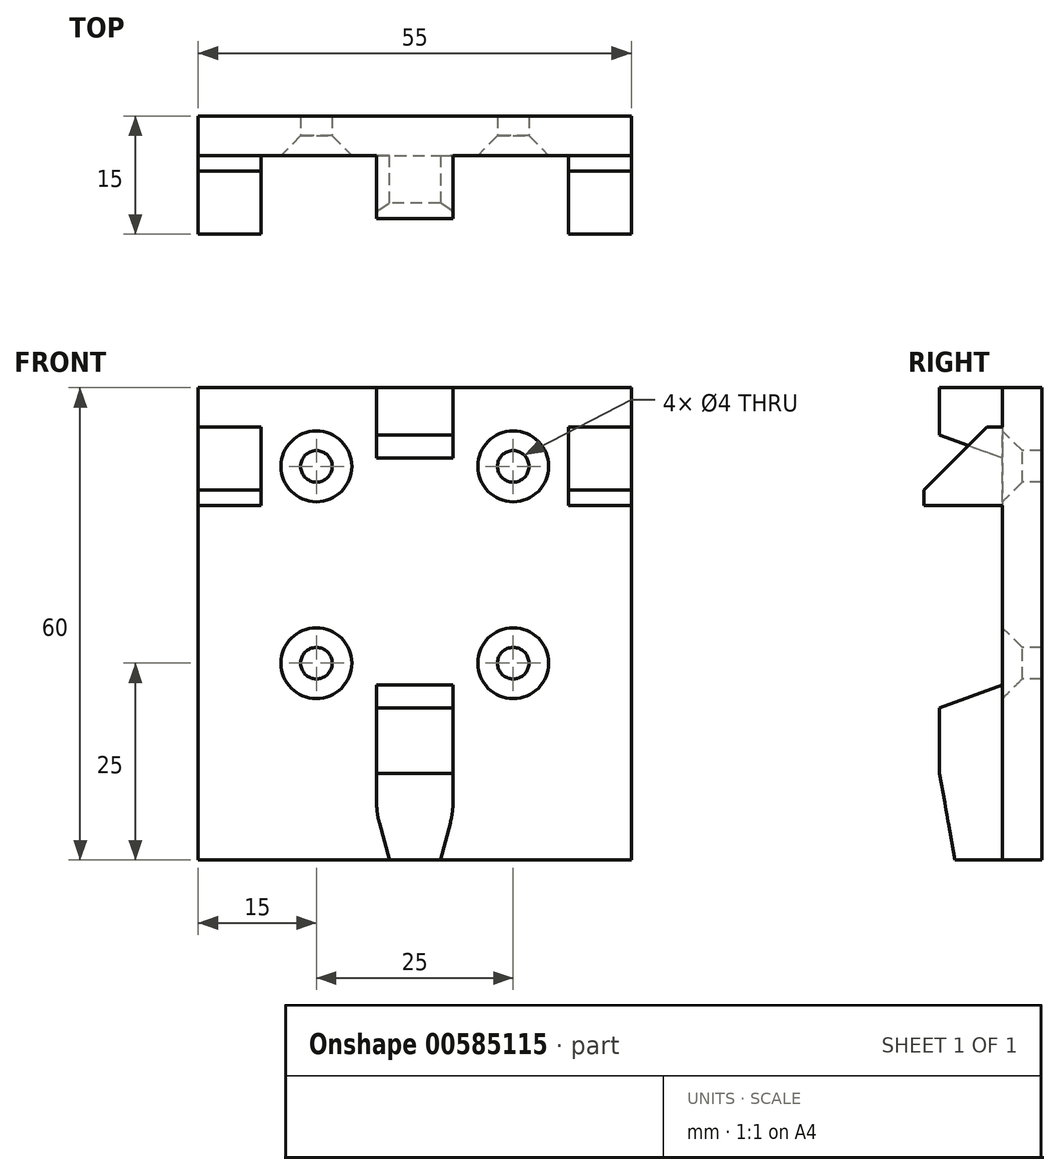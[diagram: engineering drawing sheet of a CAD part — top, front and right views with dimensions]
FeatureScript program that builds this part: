
annotation { "Feature Type Name" : "Feature", "Feature Type Description" : "" }
export const myFeature = defineFeature(function(context is Context, id is Id, definition is map)
    precondition{}
    {
        {
            var Q0;
            Q0=qCreatedBy(makeId("Top.planeOp"),FACE);
            var sketch = newSketch(context, id + "F0", { "sketchPlane" : qUnion([Q0])});
            skLineSegment(sketch, "E0", {"start": v(27.5, 0) * mm, "end": v(27.5, 5) * mm});
            skLineSegment(sketch, "E1", {"start": v(27.5, 5) * mm, "end": v(-27.5, 5) * mm});
            skLineSegment(sketch, "E2", {"start": v(-27.5, 5) * mm, "end": v(-27.5, 0) * mm});
            skLineSegment(sketch, "E3", {"start": v(-4.85, -8) * mm, "end": v(4.85, -8) * mm});
            skPoint(sketch, "E4", {"position": v(0, 0) * mm});
            skLineSegment(sketch, "E5", {"start": v(-4.85, -8) * mm, "end": v(-4.85, 0) * mm});
            skLineSegment(sketch, "E6", {"start": v(-4.85, 0) * mm, "end": v(-27.5, 0) * mm});
            skLineSegment(sketch, "E7", {"start": v(4.85, -8) * mm, "end": v(4.85, 0) * mm});
            skLineSegment(sketch, "E8", {"start": v(4.85, 0) * mm, "end": v(27.5, 0) * mm});
            skLineSegment(sketch, "E9", {"start": v(0, -8) * mm, "end": v(0, 0) * mm, "construction": true});
            skSolve(sketch);
        }
        {
            var Q0;
            Q0=qSketchRegion(id+"F0",true);
            extrude(context, id + "F1", {"entities" : qUnion([Q0]), "depth" : 60 * mm, "offsetDistance" : 25 * mm});
        }
        {
            var Q0;
            Q0=makeQuery(id+"F1.opExtrude","SWEPT_FACE",FACE,{"disambiguationData":[OSD([sQuery(id+"F0.wireOp",EDGE,"E6")])]});
            var sketch = newSketch(context, id + "F2", { "sketchPlane" : qUnion([Q0])});
            skPoint(sketch, "E10", {"position": v(-12.5, 50) * mm});
            skPoint(sketch, "E11", {"position": v(-12.5, 25) * mm});
            skLineSegment(sketch, "E12.bottom", {"start": v(-12.5, 50) * mm, "end": v(12.5, 50) * mm});
            skLineSegment(sketch, "E12.top", {"start": v(-12.5, 25) * mm, "end": v(12.5, 25) * mm});
            skLineSegment(sketch, "E12.left", {"start": v(-12.5, 50) * mm, "end": v(-12.5, 25) * mm});
            skLineSegment(sketch, "E12.right", {"start": v(12.5, 50) * mm, "end": v(12.5, 25) * mm});
            skLineSegment(sketch, "E13", {"start": v(0, 0) * mm, "end": v(0, 25) * mm});
            skPoint(sketch, "E14", {"position": v(0, 25) * mm});
            skPoint(sketch, "E15", {"position": v(12.5, 50) * mm});
            skPoint(sketch, "E16", {"position": v(12.5, 25) * mm});
            skSolve(sketch);
        }
        {
            var Q0;
            Q0=sQuery(id+"F2.wireOp",VERTEX,"E10");
            var Q1;
            Q1=sQuery(id+"F2.wireOp",VERTEX,"E11");
            var Q2;
            Q2=sQuery(id+"F2.wireOp",VERTEX,"E15");
            var Q3;
            Q3=sQuery(id+"F2.wireOp",VERTEX,"E16");
            var Q4;
            Q4=makeQuery(id+"F1.opExtrude","SWEPT_BODY",BODY,{"disambiguationData":[OSD([sQuery(id+"F0.wireOp",EDGE,"E0"),sQuery(id+"F0.wireOp",EDGE,"E1"),sQuery(id+"F0.wireOp",EDGE,"E2"),sQuery(id+"F0.wireOp",EDGE,"E3"),sQuery(id+"F0.wireOp",EDGE,"E5"),sQuery(id+"F0.wireOp",EDGE,"E6"),sQuery(id+"F0.wireOp",EDGE,"E7"),sQuery(id+"F0.wireOp",EDGE,"E8")])]});
            hole(context, id + "F3", {"style" : HoleStyle.C_SINK, "endStyle" : HoleEndStyle.THROUGH, "holeDiameter" : 4 * mm, "cSinkDiameter" : 9 * mm, "cSinkAngle" : 90 * degree, "majorDiameter" : 5 * mm, "isTappedThrough" : true, "tappedDepth" : 12 * mm, "tapClearance" : 3, "locations" : qUnion([Q0, Q1, Q2, Q3]), "scope" : qUnion([Q4])});
        }
        {
            var Q0;
            Q0=makeQuery(id+"F1.opExtrude","CAP_EDGE",EDGE,{"disambiguationData":[OSD([sQuery(id+"F0.wireOp",EDGE,"nqP1lGa1-t7VV-MA4u-jtXe-7mKQE282fZzU")])],"isStart":false});
            var Q1;
            Q1=makeQuery(id+"F1.opExtrude","CAP_EDGE",EDGE,{"disambiguationData":[OSD([sQuery(id+"F0.wireOp",EDGE,"LDgyhp3F-4NZv-x4su-AgHX-1yxxAMKI0rfL")])],"isStart":false});
            var Q2;
            Q2=makeQuery(id+"F1.opExtrude","CAP_EDGE",EDGE,{"disambiguationData":[OSD([sQuery(id+"F0.wireOp",EDGE,"E7")])],"isStart":true});
            var Q3;
            Q3=makeQuery(id+"F1.opExtrude","CAP_EDGE",EDGE,{"disambiguationData":[OSD([sQuery(id+"F0.wireOp",EDGE,"E5")])],"isStart":true});
            chamfer(context, id + "F4", {"entities" : qUnion([Q0, Q1, Q2, Q3]), "chamferType" : ChamferType.OFFSET_ANGLE, "width" : 6 * mm, "oppositeDirection" : false, "angle" : 15 * degree, "tangentPropagation" : true});
        }
        {
            var Q0;
            Q0=makeQuery(id+"F1.opExtrude","SWEPT_FACE",FACE,{"disambiguationData":[OSD([sQuery(id+"F0.wireOp",EDGE,"E6")])]});
            var sketch = newSketch(context, id + "F5", { "sketchPlane" : qUnion([Q0])});
            skLineSegment(sketch, "E17.bottom", {"start": v(-27.5, 55) * mm, "end": v(-19.5, 55) * mm});
            skLineSegment(sketch, "E17.top", {"start": v(-27.5, 45) * mm, "end": v(-19.5, 45) * mm});
            skLineSegment(sketch, "E17.left", {"start": v(-27.5, 55) * mm, "end": v(-27.5, 45) * mm});
            skLineSegment(sketch, "E17.right", {"start": v(-19.5, 55) * mm, "end": v(-19.5, 45) * mm});
            skLineSegment(sketch, "E18.bottom", {"start": v(27.5, 55) * mm, "end": v(19.5, 55) * mm});
            skLineSegment(sketch, "E18.top", {"start": v(27.5, 45) * mm, "end": v(19.5, 45) * mm});
            skLineSegment(sketch, "E18.left", {"start": v(27.5, 55) * mm, "end": v(27.5, 45) * mm});
            skLineSegment(sketch, "E18.right", {"start": v(19.5, 55) * mm, "end": v(19.5, 45) * mm});
            skLineSegment(sketch, "E19", {"start": v(-27.5, 30) * mm, "end": v(-7.31, 30) * mm, "construction": true});
            skSolve(sketch);
        }
        {
            var Q0;
            {var subQ0=sQuery(id+"F0.wireOp",EDGE,"E5");Q0=makeQuery(id+"F4.opChamfer","BLEND_EDGE",EDGE,{"blendedFrom":[makeQuery(id+"F1.opExtrude","CAP_EDGE",EDGE,{"disambiguationData":[OSD([subQ0])],"isStart":true}),makeQuery(id+"F1.opExtrude","SWEPT_FACE",FACE,{"disambiguationData":[OSD([subQ0])]})],"blendedInto":[makeQuery(id+"F1.opExtrude","SWEPT_FACE",FACE,{"disambiguationData":[OSD([subQ0])]})]});}
            var Q1;
            {var subQ0=sQuery(id+"F0.wireOp",EDGE,"E7");Q1=makeQuery(id+"F4.opChamfer","BLEND_EDGE",EDGE,{"blendedFrom":[makeQuery(id+"F1.opExtrude","CAP_EDGE",EDGE,{"disambiguationData":[OSD([subQ0])],"isStart":true}),makeQuery(id+"F1.opExtrude","SWEPT_FACE",FACE,{"disambiguationData":[OSD([subQ0])]})],"blendedInto":[makeQuery(id+"F1.opExtrude","SWEPT_FACE",FACE,{"disambiguationData":[OSD([subQ0])]})]});}
            fillet(context, id + "F6", {"entities" : qUnion([Q0, Q1]), "tangentPropagation" : true, "radius" : 10 * mm, "defaultsChanged" : true, "vertexSettings" : [], "allowEdgeOverflow" : false});
        }
        {
            var Q0;
            Q0=qSketchRegion(id+"F5",true);
            extrude(context, id + "F7", {"entities" : qUnion([Q0]), "operationType" : NewBodyOperationType.ADD, "depth" : 10 * mm, "offsetDistance" : 25 * mm});
        }
        {
            var Q0;
            Q0=makeQuery(id+"F7.opExtrude","CAP_EDGE",EDGE,{"disambiguationData":[OSD([sQuery(id+"F5.wireOp",EDGE,"E17.bottom")])],"isStart":false});
            var Q1;
            Q1=makeQuery(id+"F7.opExtrude","CAP_EDGE",EDGE,{"disambiguationData":[OSD([sQuery(id+"F5.wireOp",EDGE,"E18.bottom")])],"isStart":false});
            chamfer(context, id + "F8", {"entities" : qUnion([Q0, Q1]), "width" : 8 * mm, "tangentPropagation" : true});
        }
        {
            var Q0;
            Q0=makeQuery(id+"F1.opExtrude","SWEPT_FACE",FACE,{"disambiguationData":[OSD([sQuery(id+"F0.wireOp",EDGE,"E7")])]});
            var sketch = newSketch(context, id + "F9", { "sketchPlane" : qUnion([Q0])});
            skLineSegment(sketch, "E20", {"start": v(-8, 54) * mm, "end": v(0, 51.09) * mm});
            skLineSegment(sketch, "E21", {"start": v(0, 51.09) * mm, "end": v(0, 22.23) * mm});
            skLineSegment(sketch, "E22", {"start": v(0, 22.23) * mm, "end": v(-8, 19.32) * mm});
            skLineSegment(sketch, "E23", {"start": v(-8, 19.32) * mm, "end": v(-8, 54) * mm});
            skSolve(sketch);
        }
        {
            var Q0;
            Q0 = qSketchRegion(id + "F9", true);
            extrude(context, id + "F10", {"entities" : qUnion([Q0]), "operationType" : NewBodyOperationType.REMOVE, "endBound" : BoundingType.UP_TO_NEXT, "oppositeDirection" : true, "depth" : 25 * mm, "offsetDistance" : 25 * mm});
        }
        {
            var Q0;
            Q0=makeQuery(id+"F1.opExtrude","CAP_EDGE",EDGE,{"disambiguationData":[OSD([sQuery(id+"F0.wireOp",EDGE,"E3")])],"isStart":true});
            chamfer(context, id + "F11", {"entities" : qUnion([Q0]), "chamferType" : ChamferType.OFFSET_ANGLE, "width" : 11 * mm, "oppositeDirection" : false, "angle" : 10 * degree, "tangentPropagation" : true});
        }
    });
